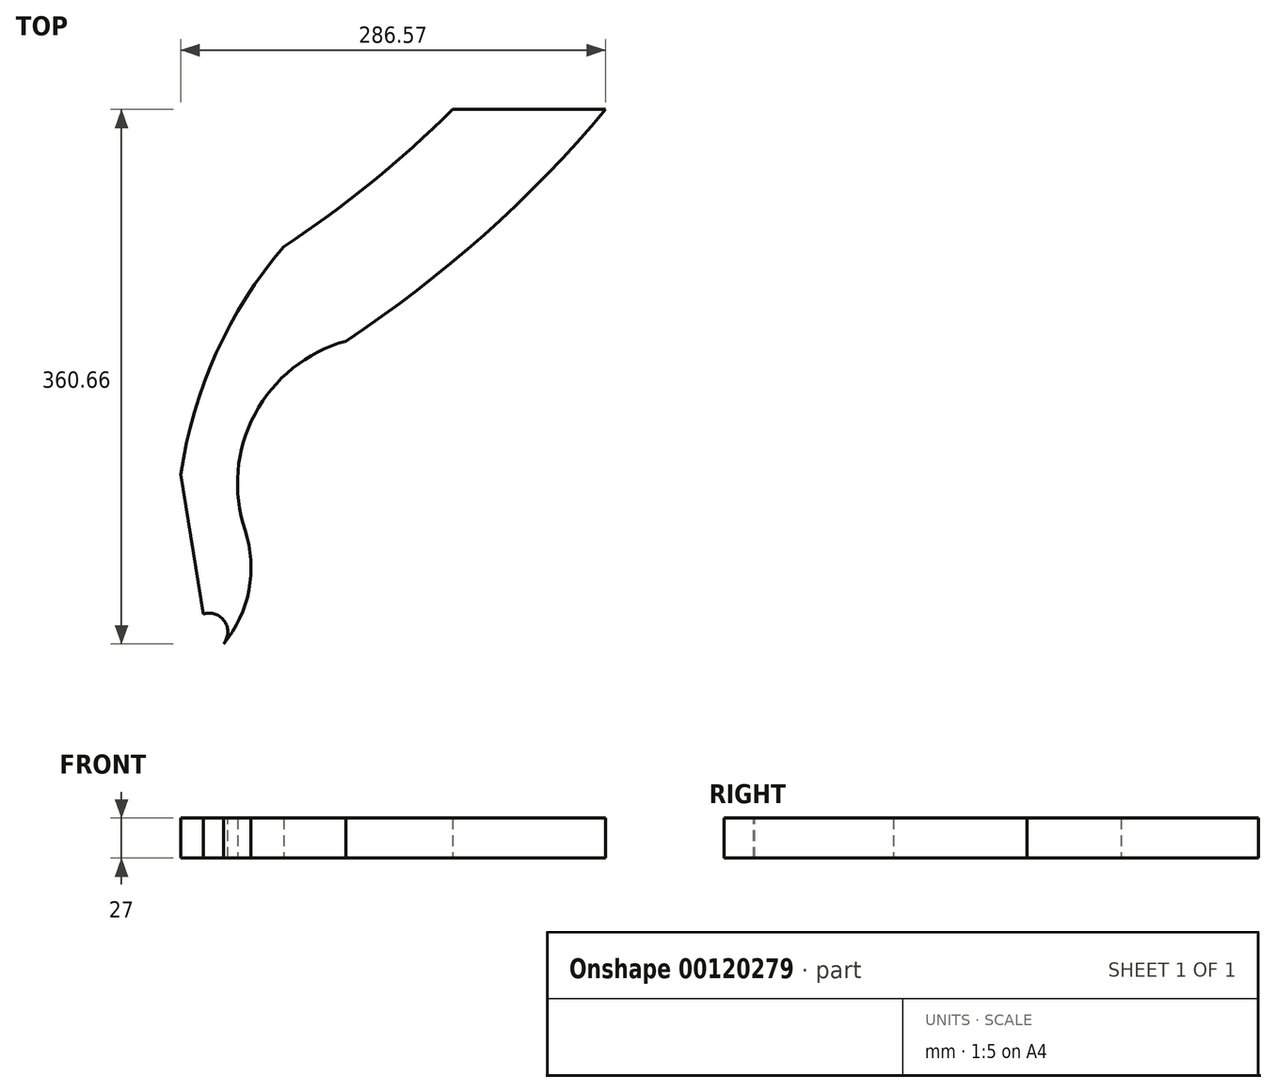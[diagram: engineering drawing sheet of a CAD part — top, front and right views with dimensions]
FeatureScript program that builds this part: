
annotation { "Feature Type Name" : "Feature", "Feature Type Description" : "" }
export const myFeature = defineFeature(function(context is Context, id is Id, definition is map)
    precondition{}
    {
        {
            var Q0;
            Q0=qCreatedBy(makeId("Top.planeOp"),FACE);
            var sketch = newSketch(context, id + "F0", { "sketchPlane" : qUnion([Q0])});
            skLineSegment(sketch, "E0.0.0", {"start": v(220, 203.8) * mm, "end": v(331.98, 180.9) * mm});
            skArc(sketch, "E0.0.1", {"start": v(331.98, 180.9) * mm, "mid": v(297.76, 202.02) * mm, "end": v(260.02, 215.9) * mm});
            skArc(sketch, "E0.0.2", {"start": v(260.02, 215.9) * mm, "mid": v(247.79, 214.8) * mm, "end": v(240.33, 224.55) * mm});
            skArc(sketch, "E0.0.3", {"start": v(240.33, 224.55) * mm, "mid": v(186.05, 230.45) * mm, "end": v(134.4, 212.72) * mm});
            skArc(sketch, "E0.0.4", {"start": v(134.4, 212.72) * mm, "mid": v(96.68, 191.93) * mm, "end": v(57.18, 174.71) * mm});
            skArc(sketch, "E0.0.5", {"start": v(25.04, 147.5) * mm, "mid": v(38.79, 163.84) * mm, "end": v(57.18, 174.71) * mm});
            skArc(sketch, "E0.0.6", {"start": v(25.04, 147.5) * mm, "mid": v(-75.16, 14.3) * mm, "end": v(-203.06, -92.57) * mm});
            skArc(sketch, "E0.0.7", {"start": v(-272.45, -246.2) * mm, "mid": v(-248.6, -164.48) * mm, "end": v(-203.06, -92.57) * mm});
            skLineSegment(sketch, "E0.0.8", {"start": v(-272.45, -246.2) * mm, "end": v(-253.42, -365.24) * mm});
            skArc(sketch, "E0.0.9", {"start": v(-253.42, -365.24) * mm, "mid": v(-248.03, -364.04) * mm, "end": v(-243.66, -360.66) * mm});
            skArc(sketch, "E0.0.10", {"start": v(-229.15, -283.97) * mm, "mid": v(-226.47, -324.2) * mm, "end": v(-243.66, -360.66) * mm});
            skArc(sketch, "E0.0.11", {"start": v(-229.15, -283.97) * mm, "mid": v(-222.5, -205.59) * mm, "end": v(-161.23, -156.26) * mm});
            skArc(sketch, "E0.0.12", {"start": v(103.14, 130.83) * mm, "mid": v(-11.34, -29.02) * mm, "end": v(-161.23, -156.26) * mm});
            skArc(sketch, "E0.0.13", {"start": v(103.14, 130.83) * mm, "mid": v(147, 190.65) * mm, "end": v(220, 203.8) * mm});
            skSolve(sketch);
        }
        {
            var Q0;
            Q0=makeQuery(id+"F0.imprint","IMPRINT",FACE,{"disambiguationData":[TD([[makeQuery(id+"F0.imprint","IMPRINT",EDGE,{"derivedFrom":sQuery(id+"F0.wireOp",EDGE,"E0.0.0")}),1.0]])]});
            extrude(context, id + "F1", {"entities" : qUnion([Q0]), "depth" : 27 * mm});
        }
        {
            var Q0;
            Q0=qCreatedBy(makeId("Top.planeOp"),FACE);
            var sketch = newSketch(context, id + "F2", { "sketchPlane" : qUnion([Q0])});
            skLineSegment(sketch, "E1.bottom", {"start": v(79.64, 0) * mm, "end": v(-323.44, 0) * mm});
            skLineSegment(sketch, "E1.top", {"start": v(79.64, -389.7) * mm, "end": v(-323.44, -389.7) * mm});
            skLineSegment(sketch, "E1.left", {"start": v(79.64, 0) * mm, "end": v(79.64, -389.7) * mm});
            skLineSegment(sketch, "E1.right", {"start": v(-323.44, 0) * mm, "end": v(-323.44, -389.7) * mm});
            skSolve(sketch);
        }
        {
            var Q0;
            Q0=makeQuery(id+"F1.opExtrude","CAP_FACE",FACE,{"disambiguationData":[OSD([sQuery(id+"F0.wireOp",EDGE,"E0.0.0"),sQuery(id+"F0.wireOp",EDGE,"E0.0.1"),sQuery(id+"F0.wireOp",EDGE,"E0.0.2"),sQuery(id+"F0.wireOp",EDGE,"E0.0.3"),sQuery(id+"F0.wireOp",EDGE,"E0.0.4"),sQuery(id+"F0.wireOp",EDGE,"E0.0.5"),sQuery(id+"F0.wireOp",EDGE,"E0.0.6"),sQuery(id+"F0.wireOp",EDGE,"E0.0.7"),sQuery(id+"F0.wireOp",EDGE,"E0.0.8"),sQuery(id+"F0.wireOp",EDGE,"E0.0.9"),sQuery(id+"F0.wireOp",EDGE,"E0.0.10"),sQuery(id+"F0.wireOp",EDGE,"E0.0.11"),sQuery(id+"F0.wireOp",EDGE,"E0.0.12"),sQuery(id+"F0.wireOp",EDGE,"E0.0.13")])],"isStart":false});
            var sketch = newSketch(context, id + "F3", { "sketchPlane" : qUnion([Q0])});
            skArc(sketch, "E2.0", {"start": v(-253.42, -365.24) * mm, "mid": v(-248.03, -364.04) * mm, "end": v(-243.66, -360.66) * mm});
            skCircle(sketch, "E3", {"center": v(-253.42, -352.54) * mm, "radius": 12.7 * mm});
            skSolve(sketch);
        }
        {
            var Q0;
            Q0 = qSketchRegion(id + "F3", true);
            extrude(context, id + "F4", {"entities" : qUnion([Q0]), "operationType" : NewBodyOperationType.REMOVE, "oppositeDirection" : true, "depth" : 29.14 * mm});
        }
        {
            var Q0;
            Q0=makeQuery(id+"F2.imprint","IMPRINT",FACE,{"disambiguationData":[TD([[makeQuery(id+"F2.imprint","IMPRINT",EDGE,{"derivedFrom":sQuery(id+"F2.wireOp",EDGE,"E1.bottom")}),1.0]])]});
            var sketch = newSketch(context, id + "F5", { "sketchPlane" : qUnion([Q0])});
            skLineSegment(sketch, "E4.bottom", {"start": v(-184.91, 0) * mm, "end": v(371.34, 0) * mm});
            skLineSegment(sketch, "E4.top", {"start": v(-184.91, 232.42) * mm, "end": v(371.34, 232.42) * mm});
            skLineSegment(sketch, "E4.left", {"start": v(-184.91, 0) * mm, "end": v(-184.91, 232.42) * mm});
            skLineSegment(sketch, "E4.right", {"start": v(371.34, 0) * mm, "end": v(371.34, 232.42) * mm});
            skSolve(sketch);
        }
        {
            var Q0;
            Q0 = qSketchRegion(id + "F5", true);
            extrude(context, id + "F6", {"entities" : qUnion([Q0]), "operationType" : NewBodyOperationType.REMOVE, "depth" : 50 * mm});
        }
    });
